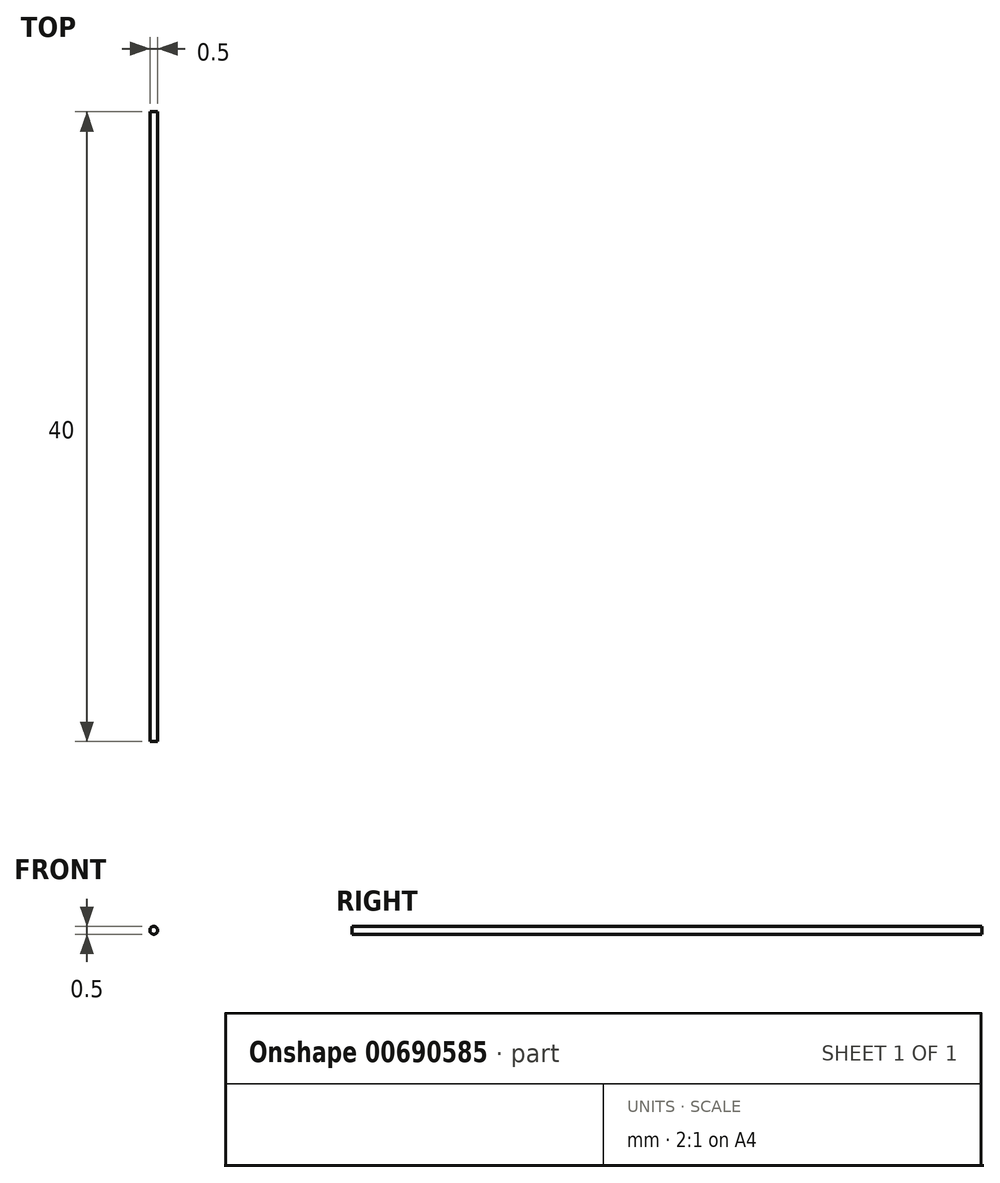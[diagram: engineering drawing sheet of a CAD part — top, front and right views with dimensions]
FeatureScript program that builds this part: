
annotation { "Feature Type Name" : "Feature", "Feature Type Description" : "" }
export const myFeature = defineFeature(function(context is Context, id is Id, definition is map)
    precondition{}
    {
        {
            var Q0;
            Q0=qCreatedBy(makeId("Front.planeOp"),FACE);
            var sketch = newSketch(context, id + "F0", { "sketchPlane" : qUnion([Q0])});
            skCircle(sketch, "E0", {"center": v(0, 0) * mm, "radius": 0.25 * mm});
            skSolve(sketch);
        }
        {
            var Q0;
            Q0 = qSketchRegion(id + "F0", true);
            extrude(context, id + "F1", {"entities" : qUnion([Q0]), "depth" : 40 * mm, "offsetDistance" : 25 * mm});
        }
    });
